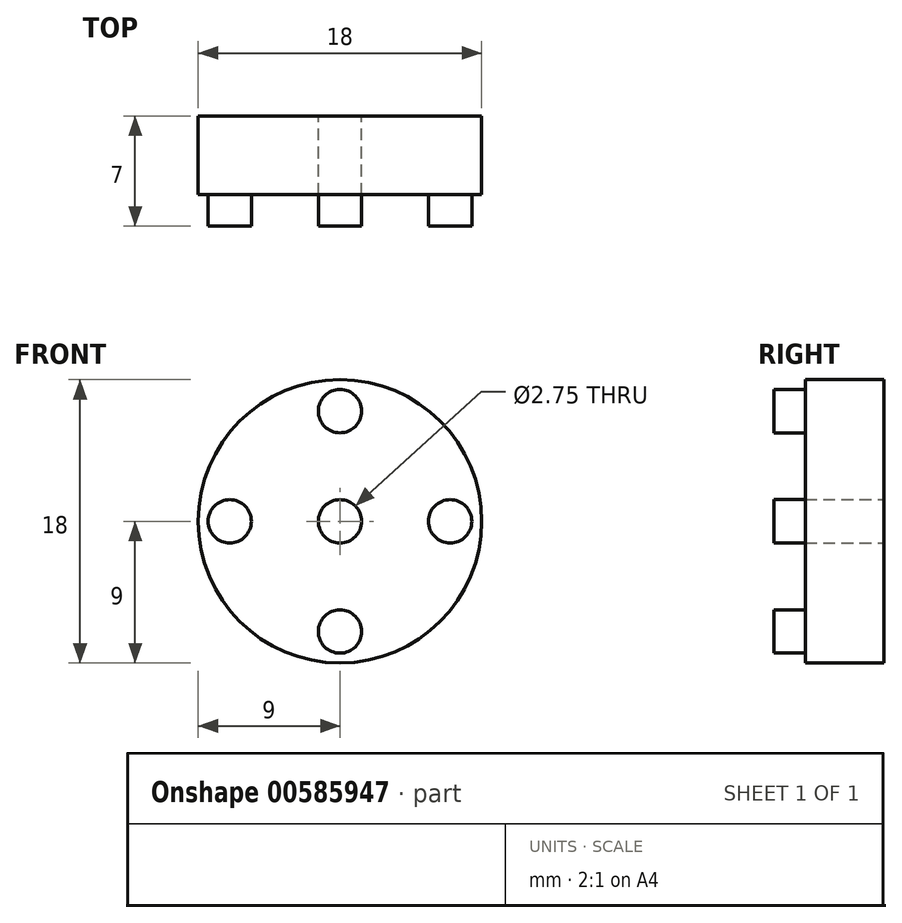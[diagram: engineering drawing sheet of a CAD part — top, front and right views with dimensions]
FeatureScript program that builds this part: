
annotation { "Feature Type Name" : "Feature", "Feature Type Description" : "" }
export const myFeature = defineFeature(function(context is Context, id is Id, definition is map)
    precondition{}
    {
        {
            var Q0;
            Q0=qCreatedBy(makeId("Front.planeOp"),FACE);
            var sketch = newSketch(context, id + "F0", { "sketchPlane" : qUnion([Q0])});
            skCircle(sketch, "E0", {"center": v(0, 0) * mm, "radius": 1.38 * mm});
            skCircle(sketch, "E1", {"center": v(0, 0) * mm, "radius": 7 * mm, "construction": true});
            skLineSegment(sketch, "E2", {"start": v(0, 0) * mm, "end": v(7, 0) * mm, "construction": true});
            skCircle(sketch, "E3", {"center": v(7, 0) * mm, "radius": 1.38 * mm});
            skCircle(sketch, "E4", {"center": v(0, 0) * mm, "radius": 9 * mm});
            skCircle(sketch, "E5.1.0", {"center": v(0, 7) * mm, "radius": 1.38 * mm});
            skCircle(sketch, "E5.2.0", {"center": v(-7, 0) * mm, "radius": 1.38 * mm});
            skCircle(sketch, "E5.3.0", {"center": v(0, -7) * mm, "radius": 1.38 * mm});
            skCircle(sketch, "E6", {"center": v(0, 0) * mm, "radius": 4 * mm});
            skLineSegment(sketch, "E7", {"start": v(1.23, 0.8) * mm, "end": v(1.23, -0.95) * mm});
            skSolve(sketch);
        }
        {
            var Q0;
            Q0=makeQuery(id+"F0.imprint","IMPRINT",FACE,{"disambiguationData":[TD([[makeQuery(id+"F0.imprint","IMPRINT",EDGE,{"derivedFrom":sQuery(id+"F0.wireOp",EDGE,"E0")}),-1.0]])]});
            var Q1;
            Q1=makeQuery(id+"F0.imprint","IMPRINT",FACE,{"disambiguationData":[TD([[makeQuery(id+"F0.imprint","IMPRINT",EDGE,{"derivedFrom":sQuery(id+"F0.wireOp",EDGE,"E3")}),-1.0]])]});
            var Q2;
            {var subQ0=sQuery(id+"F0.wireOp",EDGE,"E0");var subQ1=makeQuery(id+"F0.imprint","IMPRINT",VERTEX,{"derivedFrom":subQ0});Q2=makeQuery(id+"F0.imprint","IMPRINT",FACE,{"disambiguationData":[TD([[makeQuery(id+"F0.imprint","IMPRINT",EDGE,{"disambiguationData":[TD([[subQ1,1.0]])],"derivedFrom":subQ0}),1.0]])]});}
            extrude(context, id + "F1", {"entities" : qUnion([Q0, Q1, Q2]), "depth" : 2 * mm, "offsetDistance" : 25 * mm});
        }
        {
            var Q0;
            Q0=makeQuery(id+"F0.imprint","IMPRINT",FACE,{"disambiguationData":[TD([[makeQuery(id+"F0.imprint","IMPRINT",EDGE,{"derivedFrom":sQuery(id+"F0.wireOp",EDGE,"E5.2.0")}),1.0]])]});
            var Q1;
            Q1=makeQuery(id+"F0.imprint","IMPRINT",FACE,{"disambiguationData":[TD([[makeQuery(id+"F0.imprint","IMPRINT",EDGE,{"derivedFrom":sQuery(id+"F0.wireOp",EDGE,"E5.1.0")}),1.0]])]});
            var Q2;
            Q2=makeQuery(id+"F0.imprint","IMPRINT",FACE,{"disambiguationData":[TD([[makeQuery(id+"F0.imprint","IMPRINT",EDGE,{"derivedFrom":sQuery(id+"F0.wireOp",EDGE,"E3")}),1.0]])]});
            var Q3;
            Q3=makeQuery(id+"F0.imprint","IMPRINT",FACE,{"disambiguationData":[TD([[makeQuery(id+"F0.imprint","IMPRINT",EDGE,{"derivedFrom":sQuery(id+"F0.wireOp",EDGE,"E5.3.0")}),1.0]])]});
            extrude(context, id + "F2", {"entities" : qUnion([Q0, Q1, Q2, Q3]), "operationType" : NewBodyOperationType.ADD, "depth" : 4 * mm, "offsetDistance" : 25 * mm});
        }
        {
            var Q0;
            Q0=makeQuery(id+"F0.imprint","IMPRINT",FACE,{"disambiguationData":[TD([[makeQuery(id+"F0.imprint","IMPRINT",EDGE,{"derivedFrom":sQuery(id+"F0.wireOp",EDGE,"E0")}),-1.0]])]});
            var Q1;
            Q1=makeQuery(id+"F0.imprint","IMPRINT",FACE,{"disambiguationData":[TD([[makeQuery(id+"F0.imprint","IMPRINT",EDGE,{"derivedFrom":sQuery(id+"F0.wireOp",EDGE,"E3")}),-1.0]])]});
            var Q2;
            Q2=makeQuery(id+"F0.imprint","IMPRINT",FACE,{"disambiguationData":[TD([[makeQuery(id+"F0.imprint","IMPRINT",EDGE,{"derivedFrom":sQuery(id+"F0.wireOp",EDGE,"E5.1.0")}),1.0]])]});
            var Q3;
            Q3=makeQuery(id+"F0.imprint","IMPRINT",FACE,{"disambiguationData":[TD([[makeQuery(id+"F0.imprint","IMPRINT",EDGE,{"derivedFrom":sQuery(id+"F0.wireOp",EDGE,"E3")}),1.0]])]});
            var Q4;
            Q4=makeQuery(id+"F0.imprint","IMPRINT",FACE,{"disambiguationData":[TD([[makeQuery(id+"F0.imprint","IMPRINT",EDGE,{"derivedFrom":sQuery(id+"F0.wireOp",EDGE,"E5.3.0")}),1.0]])]});
            var Q5;
            Q5=makeQuery(id+"F0.imprint","IMPRINT",FACE,{"disambiguationData":[TD([[makeQuery(id+"F0.imprint","IMPRINT",EDGE,{"derivedFrom":sQuery(id+"F0.wireOp",EDGE,"E5.2.0")}),1.0]])]});
            var Q6;
            {var subQ0=sQuery(id+"F0.wireOp",EDGE,"E0");var subQ1=makeQuery(id+"F0.imprint","IMPRINT",VERTEX,{"derivedFrom":subQ0});Q6=makeQuery(id+"F0.imprint","IMPRINT",FACE,{"disambiguationData":[TD([[makeQuery(id+"F0.imprint","IMPRINT",EDGE,{"disambiguationData":[TD([[subQ1,1.0]])],"derivedFrom":subQ0}),1.0]])]});}
            extrude(context, id + "F3", {"entities" : qUnion([Q0, Q1, Q2, Q3, Q4, Q5, Q6]), "operationType" : NewBodyOperationType.ADD, "oppositeDirection" : true, "depth" : 3 * mm, "offsetDistance" : 25 * mm});
        }
    });
